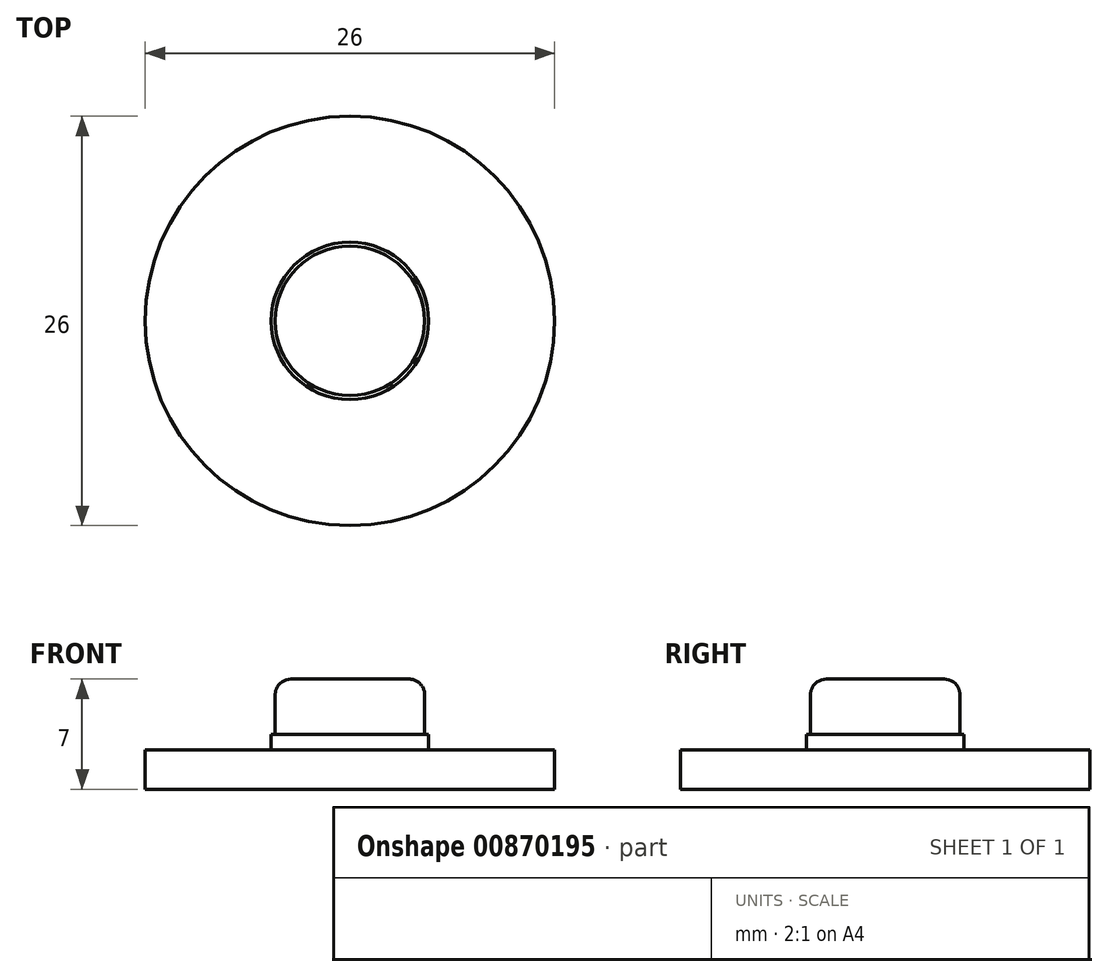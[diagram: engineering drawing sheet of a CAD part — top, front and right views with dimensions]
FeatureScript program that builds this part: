
annotation { "Feature Type Name" : "Feature", "Feature Type Description" : "" }
export const myFeature = defineFeature(function(context is Context, id is Id, definition is map)
    precondition{}
    {
        {
            var Q0;
            Q0=qCreatedBy(makeId("Top.planeOp"),FACE);
            var sketch = newSketch(context, id + "F0", { "sketchPlane" : qUnion([Q0])});
            skCircle(sketch, "E0", {"center": v(0, 0) * mm, "radius": 13 * mm});
            skSolve(sketch);
        }
        {
            var Q0;
            Q0=makeQuery(id+"F0.imprint","IMPRINT",FACE,{"disambiguationData":[TD([[makeQuery(id+"F0.imprint","IMPRINT",EDGE,{"derivedFrom":sQuery(id+"F0.wireOp",EDGE,"E0")}),1.0]])]});
            extrude(context, id + "F1", {"entities" : qUnion([Q0]), "depth" : 2.5 * mm, "offsetDistance" : 25 * mm});
        }
        {
            var Q0;
            Q0=qCreatedBy(makeId("Top.planeOp"),FACE);
            var sketch = newSketch(context, id + "F2", { "sketchPlane" : qUnion([Q0])});
            skCircle(sketch, "E1", {"center": v(0, 0) * mm, "radius": 5 * mm});
            skSolve(sketch);
        }
        {
            var Q0;
            Q0 = qSketchRegion(id + "F2", true);
            extrude(context, id + "F3", {"entities" : qUnion([Q0]), "operationType" : NewBodyOperationType.ADD, "depth" : 3.5 * mm, "offsetDistance" : 25 * mm});
        }
        {
            var Q0;
            Q0=qCreatedBy(makeId("Top.planeOp"),FACE);
            var sketch = newSketch(context, id + "F4", { "sketchPlane" : qUnion([Q0])});
            skCircle(sketch, "E2", {"center": v(0, 0) * mm, "radius": 4.75 * mm});
            skSolve(sketch);
        }
        {
            var Q0;
            Q0=makeQuery(id+"F4.imprint","IMPRINT",FACE,{"disambiguationData":[TD([[makeQuery(id+"F4.imprint","IMPRINT",EDGE,{"derivedFrom":sQuery(id+"F4.wireOp",EDGE,"E2")}),1.0]])]});
            extrude(context, id + "F5", {"entities" : qUnion([Q0]), "operationType" : NewBodyOperationType.ADD, "depth" : 7 * mm, "offsetDistance" : 25 * mm});
        }
        {
            var Q0;
            Q0=makeQuery(id+"F5.opExtrude","CAP_EDGE",EDGE,{"disambiguationData":[OSD([sQuery(id+"F4.wireOp",EDGE,"E2")])],"isStart":false});
            fillet(context, id + "F6", {"entities" : qUnion([Q0]), "radius" : 1 * mm, "tangentPropagation" : true, "allowEdgeOverflow" : false});
        }
    });
